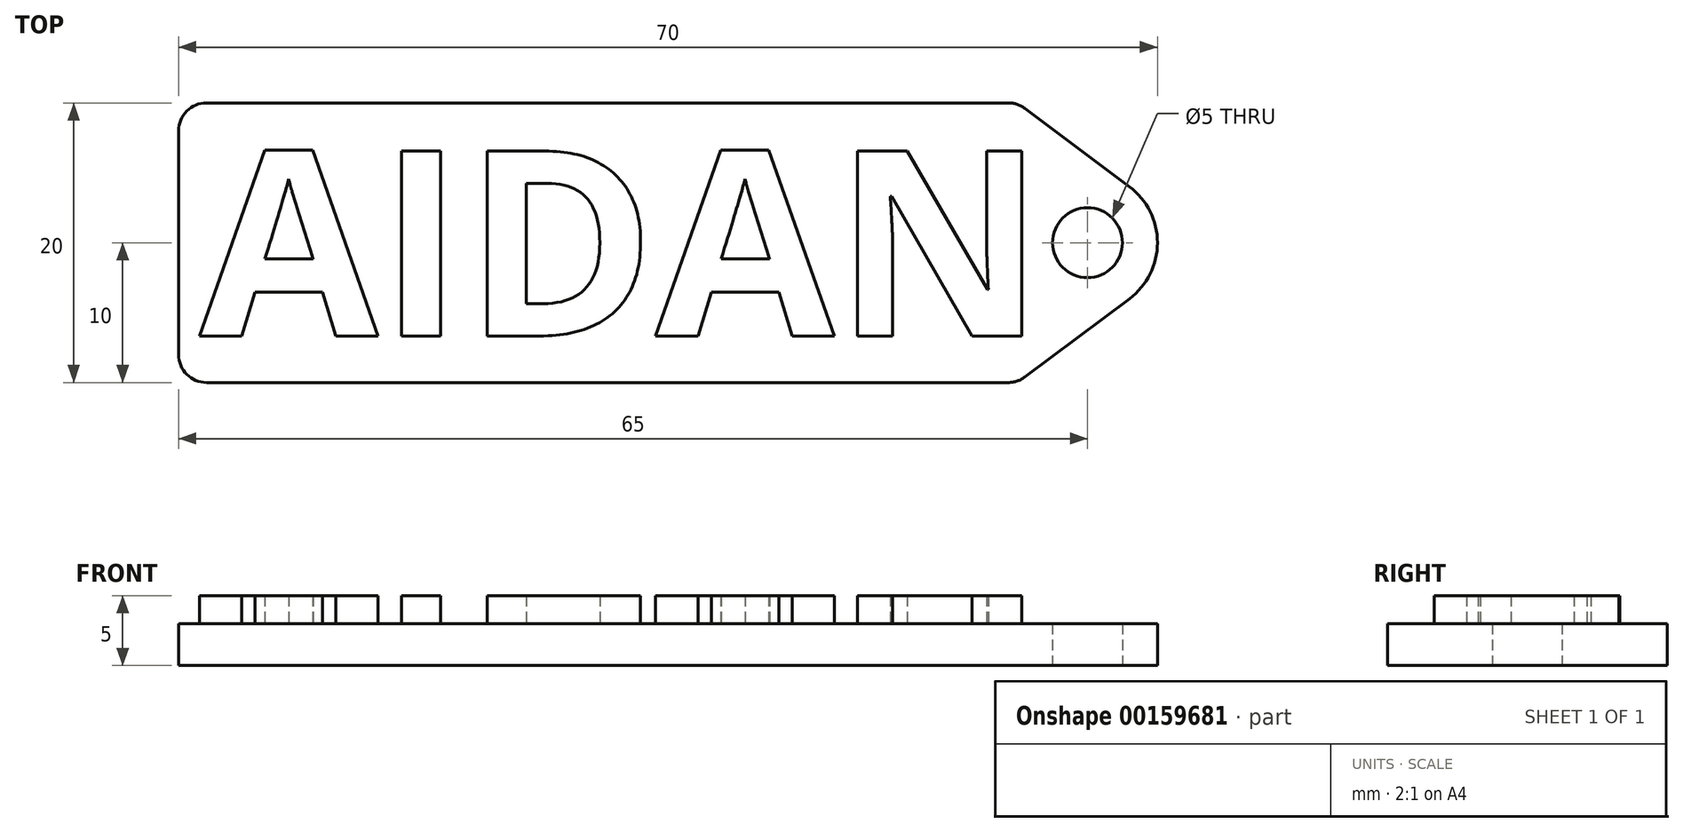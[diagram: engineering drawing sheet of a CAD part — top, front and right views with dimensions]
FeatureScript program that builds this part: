
annotation { "Feature Type Name" : "Feature", "Feature Type Description" : "" }
export const myFeature = defineFeature(function(context is Context, id is Id, definition is map)
    precondition{}
    {
        {
            var Q0;
            Q0=qCreatedBy(makeId("Top.planeOp"),FACE);
            var sketch = newSketch(context, id + "F0", { "sketchPlane" : qUnion([Q0])});
            skLineSegment(sketch, "E0.bottom", {"start": v(29.33, -10) * mm, "end": v(-28, -10) * mm});
            skLineSegment(sketch, "E0.top", {"start": v(29.33, 10) * mm, "end": v(-28, 10) * mm});
            skLineSegment(sketch, "E0.left", {"start": v(30, -10) * mm, "end": v(30, 10) * mm, "construction": true});
            skLineSegment(sketch, "E0.right", {"start": v(-30, -8) * mm, "end": v(-30, 8) * mm});
            skPoint(sketch, "E0.middle", {"position": v(0, 0) * mm});
            skCircle(sketch, "E1", {"center": v(35, 0) * mm, "radius": 2.5 * mm});
            skLineSegment(sketch, "E2", {"start": v(30.53, 9.6) * mm, "end": v(38, 4) * mm});
            skArc(sketch, "E3", {"start": v(40, 0) * mm, "mid": v(39.47, 2.24) * mm, "end": v(38, 4) * mm});
            skLineSegment(sketch, "E4.MirrorCS", {"start": v(30.53, -9.6) * mm, "end": v(38, -4) * mm});
            skArc(sketch, "E5.MirrorCS", {"start": v(40, 0) * mm, "mid": v(39.47, -2.24) * mm, "end": v(38, -4) * mm});
            skPoint(sketch, "E6.visualSharp", {"position": v(-30, 10) * mm});
            skArc(sketch, "E6.filletArc", {"start": v(-28, 10) * mm, "mid": v(-29.41, 9.41) * mm, "end": v(-30, 8) * mm});
            skPoint(sketch, "E7.visualSharp", {"position": v(-30, -10) * mm});
            skArc(sketch, "E7.filletArc", {"start": v(-30, -8) * mm, "mid": v(-29.41, -9.41) * mm, "end": v(-28, -10) * mm});
            skPoint(sketch, "E8.visualSharp", {"position": v(30, 10) * mm});
            skArc(sketch, "E8.filletArc", {"start": v(30.53, 9.6) * mm, "mid": v(29.97, 9.9) * mm, "end": v(29.33, 10) * mm});
            skPoint(sketch, "E9.visualSharp", {"position": v(30, -10) * mm});
            skArc(sketch, "E9.filletArc", {"start": v(29.33, -10) * mm, "mid": v(29.97, -9.9) * mm, "end": v(30.53, -9.6) * mm});
            skSolve(sketch);
        }
        {
            var Q0;
            Q0=makeQuery(id+"F0.imprint","IMPRINT",FACE,{"disambiguationData":[TD([[makeQuery(id+"F0.imprint","IMPRINT",EDGE,{"derivedFrom":sQuery(id+"F0.wireOp",EDGE,"E0.bottom")}),-1.0]])]});
            extrude(context, id + "F1", {"entities" : qUnion([Q0]), "depth" : 3 * mm});
        }
        {
            var Q0;
            Q0=makeQuery(id+"F1.opExtrude","CAP_FACE",FACE,{"disambiguationData":[OSD([sQuery(id+"F0.wireOp",EDGE,"E0.bottom"),sQuery(id+"F0.wireOp",EDGE,"E0.top"),sQuery(id+"F0.wireOp",EDGE,"E0.right"),sQuery(id+"F0.wireOp",EDGE,"E1"),sQuery(id+"F0.wireOp",EDGE,"E2"),sQuery(id+"F0.wireOp",EDGE,"E3"),sQuery(id+"F0.wireOp",EDGE,"E4.MirrorCS"),sQuery(id+"F0.wireOp",EDGE,"E5.MirrorCS"),sQuery(id+"F0.wireOp",EDGE,"E6.filletArc"),sQuery(id+"F0.wireOp",EDGE,"E7.filletArc"),sQuery(id+"F0.wireOp",EDGE,"E8.filletArc"),sQuery(id+"F0.wireOp",EDGE,"E9.filletArc")])],"isStart":false});
            var sketch = newSketch(context, id + "F2", { "sketchPlane" : qUnion([Q0])});
            skText(sketch, "E10", { "text": "AIDAN", "fontName": "OpenSans-Bold.ttf"});
            skPoint(sketch, "E11", {"position": v(-28.52, 0) * mm});
            const initialGuessF2  = {"E10": [-0.02852, -0.00667, 1, 0, 0.01334]};
            skSetInitialGuess(sketch, initialGuessF2);
            skSolve(sketch);
        }
        {
            var Q0;
            Q0=qSketchRegion(id+"F2",true);
            extrude(context, id + "F3", {"entities" : qUnion([Q0]), "operationType" : NewBodyOperationType.ADD, "depth" : 2 * mm});
        }
    });
